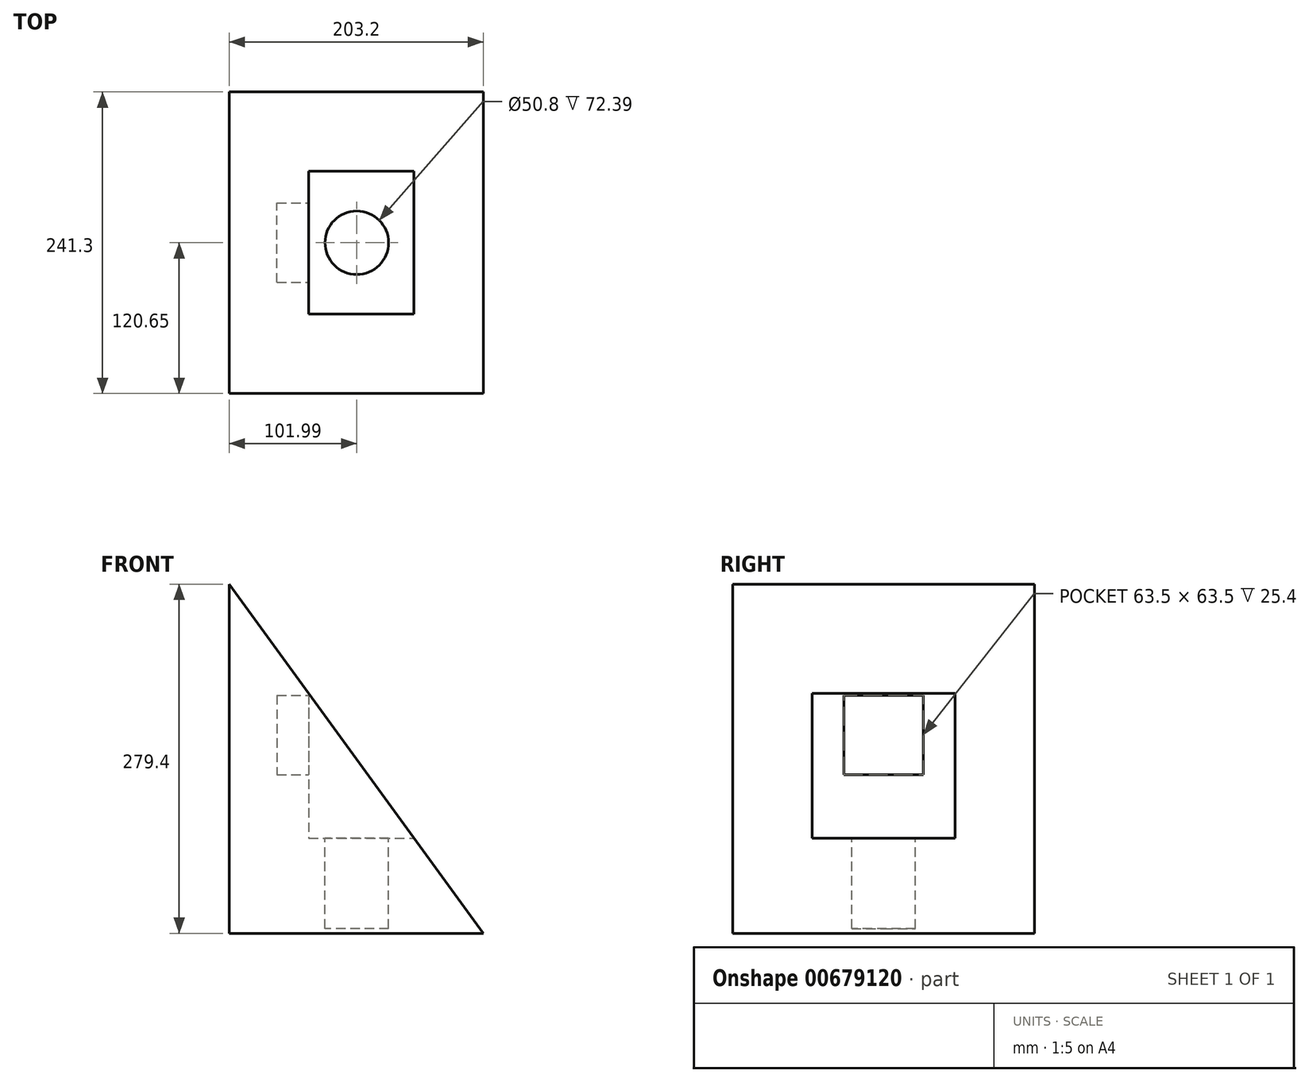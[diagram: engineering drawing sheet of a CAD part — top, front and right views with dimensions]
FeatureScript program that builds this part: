
annotation { "Feature Type Name" : "Feature", "Feature Type Description" : "" }
export const myFeature = defineFeature(function(context is Context, id is Id, definition is map)
    precondition{}
    {
        {
            var Q0;
            Q0=qCreatedBy(makeId("Front.planeOp"),FACE);
            var sketch = newSketch(context, id + "F0", { "sketchPlane" : qUnion([Q0])});
            skLineSegment(sketch, "E0", {"start": v(-102, 0) * mm, "end": v(101.2, 0) * mm});
            skLineSegment(sketch, "E1.0", {"start": v(-102, 279.4) * mm, "end": v(101.2, 279.4) * mm});
            skLineSegment(sketch, "E2", {"start": v(-102, 279.4) * mm, "end": v(-102, 0) * mm});
            skLineSegment(sketch, "E3", {"start": v(-102, 279.4) * mm, "end": v(101.2, 0) * mm});
            skLineSegment(sketch, "E4", {"start": v(101.2, 279.4) * mm, "end": v(101.2, 0) * mm});
            skSolve(sketch);
        }
        {
            var Q0;
            Q0=makeQuery(id+"F0.imprint","IMPRINT",FACE,{"disambiguationData":[TD([[makeQuery(id+"F0.imprint","IMPRINT",EDGE,{"derivedFrom":sQuery(id+"F0.wireOp",EDGE,"E0")}),1.0]])]});
            var Q1;
            Q1=makeQuery(id+"F0.imprint","IMPRINT",FACE,{"disambiguationData":[TD([[makeQuery(id+"F0.imprint","IMPRINT",EDGE,{"derivedFrom":sQuery(id+"F0.wireOp",EDGE,"E1.0")}),-1.0]])]});
            extrude(context, id + "F1", {"entities" : qUnion([Q0, Q1]), "endBound" : BoundingType.SYMMETRIC, "depth" : 241.3 * mm, "offsetDistance" : 25.4 * mm});
        }
        {
            var Q0;
            Q0=makeQuery(id+"F1.opExtrude","SWEPT_FACE",FACE,{"disambiguationData":[OSD([sQuery(id+"F0.wireOp",EDGE,"E4")])]});
            var sketch = newSketch(context, id + "F2", { "sketchPlane" : qUnion([Q0])});
            skLineSegment(sketch, "E5.bottom", {"start": v(-57.15, 215.9) * mm, "end": v(57.15, 215.9) * mm});
            skLineSegment(sketch, "E5.top", {"start": v(-57.15, 76.2) * mm, "end": v(57.15, 76.2) * mm});
            skLineSegment(sketch, "E5.left", {"start": v(-57.15, 215.9) * mm, "end": v(-57.15, 76.2) * mm});
            skLineSegment(sketch, "E5.right", {"start": v(57.15, 215.9) * mm, "end": v(57.15, 76.2) * mm});
            skLineSegment(sketch, "E6.bottom", {"start": v(-31.75, 190.5) * mm, "end": v(31.75, 190.5) * mm});
            skLineSegment(sketch, "E6.top", {"start": v(-31.75, 127) * mm, "end": v(31.75, 127) * mm});
            skLineSegment(sketch, "E6.left", {"start": v(-31.75, 190.5) * mm, "end": v(-31.75, 127) * mm});
            skLineSegment(sketch, "E6.right", {"start": v(31.75, 190.5) * mm, "end": v(31.75, 127) * mm});
            skSolve(sketch);
        }
        {
            var Q0;
            Q0=makeQuery(id+"F2.imprint","IMPRINT",FACE,{"disambiguationData":[TD([[makeQuery(id+"F2.imprint","IMPRINT",EDGE,{"derivedFrom":sQuery(id+"F2.wireOp",EDGE,"E6.bottom")}),-1.0]])]});
            var Q1;
            Q1=makeQuery(id+"F2.imprint","IMPRINT",FACE,{"disambiguationData":[TD([[makeQuery(id+"F2.imprint","IMPRINT",EDGE,{"derivedFrom":sQuery(id+"F2.wireOp",EDGE,"E5.bottom")}),-1.0]])]});
            extrude(context, id + "F3", {"entities" : qUnion([Q0, Q1]), "operationType" : NewBodyOperationType.REMOVE, "oppositeDirection" : true, "depth" : 139.7 * mm, "offsetDistance" : 25.4 * mm});
        }
        {
            var Q0;
            Q0=makeQuery(id+"F2.imprint","IMPRINT",FACE,{"disambiguationData":[TD([[makeQuery(id+"F2.imprint","IMPRINT",EDGE,{"derivedFrom":sQuery(id+"F2.wireOp",EDGE,"E6.bottom")}),-1.0]])]});
            extrude(context, id + "F4", {"entities" : qUnion([Q0]), "operationType" : NewBodyOperationType.ADD, "oppositeDirection" : true, "depth" : 165.1 * mm, "offsetDistance" : 25.4 * mm});
        }
        {
            var Q0;
            Q0=makeQuery(id+"F0.imprint","IMPRINT",FACE,{"disambiguationData":[TD([[makeQuery(id+"F0.imprint","IMPRINT",EDGE,{"derivedFrom":sQuery(id+"F0.wireOp",EDGE,"E1.0")}),-1.0]])]});
            extrude(context, id + "F5", {"entities" : qUnion([Q0]), "operationType" : NewBodyOperationType.REMOVE, "depth" : 271.53 * mm, "offsetDistance" : 25.4 * mm, "hasSecondDirection" : true, "secondDirectionOppositeDirection" : true, "secondDirectionDepth" : 305.05 * mm});
        }
        {
            var Q0;
            Q0=makeQuery(id+"F4.opExtrude","SWEPT_FACE",FACE,{"disambiguationData":[OSD([sQuery(id+"F2.wireOp",EDGE,"E6.left")])]});
            extrude(context, id + "F6", {"entities" : qUnion([Q0]), "operationType" : NewBodyOperationType.REMOVE, "oppositeDirection" : true, "depth" : 87.12 * mm, "offsetDistance" : 25.4 * mm});
        }
        {
            var Q0;
            Q0=makeQuery(id+"F2.imprint","IMPRINT",FACE,{"disambiguationData":[TD([[makeQuery(id+"F2.imprint","IMPRINT",EDGE,{"derivedFrom":sQuery(id+"F2.wireOp",EDGE,"E6.bottom")}),-1.0]])]});
            extrude(context, id + "F7", {"entities" : qUnion([Q0]), "operationType" : NewBodyOperationType.REMOVE, "oppositeDirection" : true, "depth" : 165.1 * mm, "offsetDistance" : 25.4 * mm});
        }
        {
            var Q0;
            Q0=makeQuery(id+"F3.boolean.opBoolean","COPY",FACE,{"derivedFrom":makeQuery(id+"F3.opExtrude","SWEPT_FACE",FACE,{"disambiguationData":[OSD([sQuery(id+"F2.wireOp",EDGE,"E5.top")])]})});
            var sketch = newSketch(context, id + "F8", { "sketchPlane" : qUnion([Q0])});
            skCircle(sketch, "E7", {"center": v(0, 0) * mm, "radius": 25.4 * mm});
            skSolve(sketch);
        }
        {
            var Q0;
            Q0=makeQuery(id+"F8.imprint","IMPRINT",FACE,{"disambiguationData":[TD([[makeQuery(id+"F8.imprint","IMPRINT",EDGE,{"derivedFrom":sQuery(id+"F8.wireOp",EDGE,"E7")}),1.0]])]});
            extrude(context, id + "F9", {"entities" : qUnion([Q0]), "operationType" : NewBodyOperationType.REMOVE, "oppositeDirection" : true, "depth" : 72.39 * mm, "offsetDistance" : 25.4 * mm});
        }
    });
